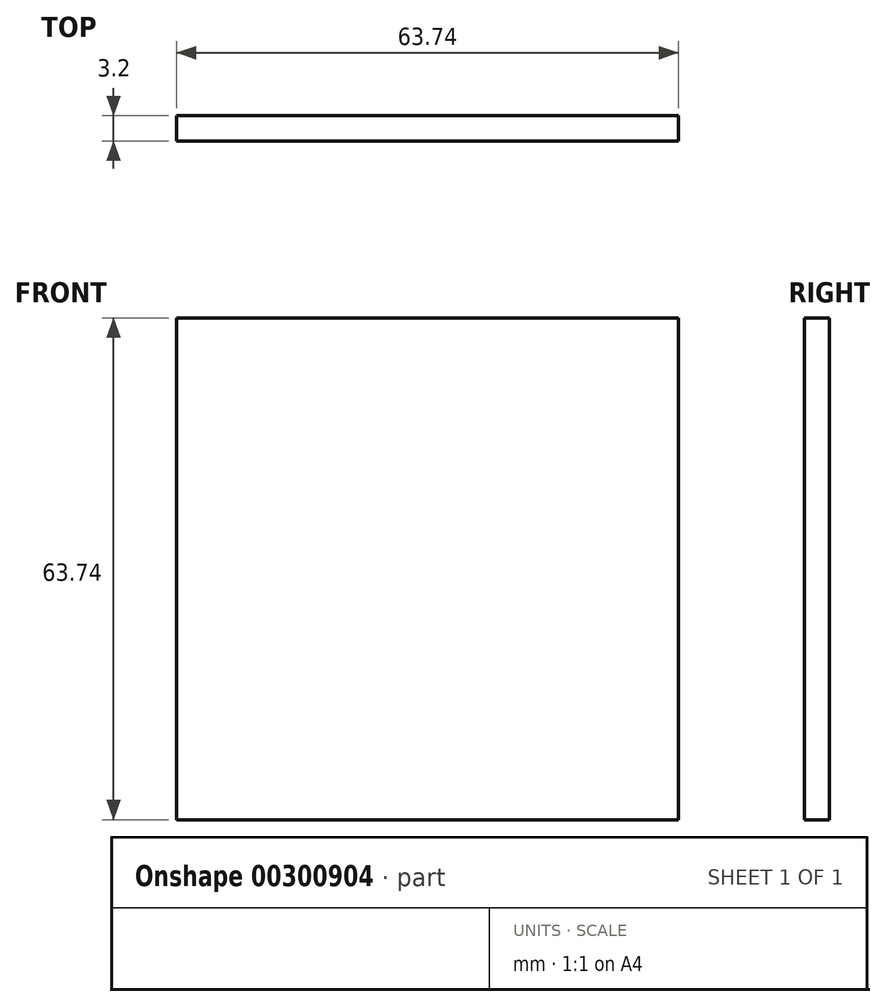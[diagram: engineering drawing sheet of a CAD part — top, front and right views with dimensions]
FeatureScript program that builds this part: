
annotation { "Feature Type Name" : "Feature", "Feature Type Description" : "" }
export const myFeature = defineFeature(function(context is Context, id is Id, definition is map)
    precondition{}
    {
        {
            var Q0;
            Q0=qCreatedBy(makeId("Front.planeOp"),FACE);
            var sketch = newSketch(context, id + "F0", { "sketchPlane" : qUnion([Q0])});
            skLineSegment(sketch, "E0.bottom", {"start": v(0, 0) * mm, "end": v(-63.74, 0) * mm});
            skLineSegment(sketch, "E0.top", {"start": v(0, 63.74) * mm, "end": v(-63.74, 63.74) * mm});
            skLineSegment(sketch, "E0.left", {"start": v(0, 0) * mm, "end": v(0, 63.74) * mm});
            skLineSegment(sketch, "E0.right", {"start": v(-63.74, 0) * mm, "end": v(-63.74, 63.74) * mm});
            skSolve(sketch);
        }
        {
            var Q0;
            Q0=makeQuery(id+"F0.imprint","IMPRINT",FACE,{"disambiguationData":[TD([[makeQuery(id+"F0.imprint","IMPRINT",EDGE,{"derivedFrom":sQuery(id+"F0.wireOp",EDGE,"E0.bottom")}),-1.0]])]});
            extrude(context, id + "F1", {"entities" : qUnion([Q0]), "depth" : 3.2 * mm});
        }
    });
